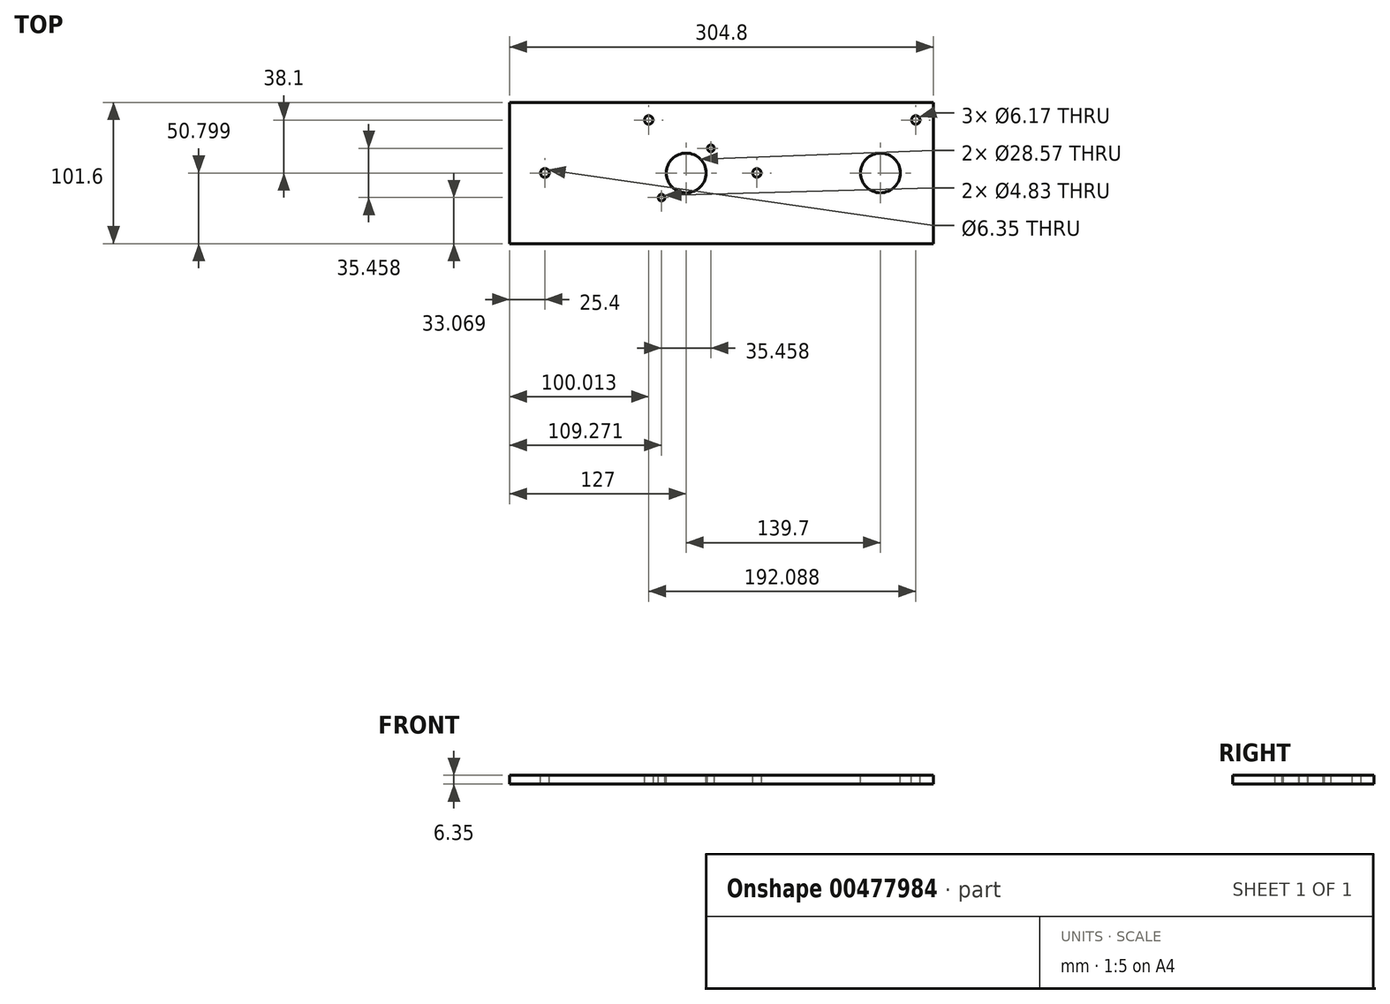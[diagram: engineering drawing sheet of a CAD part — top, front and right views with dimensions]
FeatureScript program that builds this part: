
annotation { "Feature Type Name" : "Feature", "Feature Type Description" : "" }
export const myFeature = defineFeature(function(context is Context, id is Id, definition is map)
    precondition{}
    {
        {
            var Q0;
            Q0=qCreatedBy(makeId("Top.planeOp"),FACE);
            var sketch = newSketch(context, id + "F0", { "sketchPlane" : qUnion([Q0])});
            skLineSegment(sketch, "E0.bottom", {"start": v(-72.69, 42.63) * mm, "end": v(232.11, 42.63) * mm});
            skLineSegment(sketch, "E0.top", {"start": v(-72.69, -58.97) * mm, "end": v(232.11, -58.97) * mm});
            skLineSegment(sketch, "E0.left", {"start": v(-72.69, 42.63) * mm, "end": v(-72.69, -58.97) * mm});
            skLineSegment(sketch, "E0.right", {"start": v(232.11, 42.63) * mm, "end": v(232.11, -58.97) * mm});
            skSolve(sketch);
        }
        {
            var Q0;
            Q0=makeQuery(id+"F0.imprint","IMPRINT",FACE,{"disambiguationData":[TD([[makeQuery(id+"F0.imprint","IMPRINT",EDGE,{"derivedFrom":sQuery(id+"F0.wireOp",EDGE,"E0.bottom")}),-1.0]])]});
            extrude(context, id + "F1", {"entities" : qUnion([Q0]), "depth" : 6.35 * mm});
        }
        {
            var Q0;
            Q0=makeQuery(id+"F1.opExtrude","CAP_FACE",FACE,{"disambiguationData":[OSD([sQuery(id+"F0.wireOp",EDGE,"E0.bottom"),sQuery(id+"F0.wireOp",EDGE,"E0.top"),sQuery(id+"F0.wireOp",EDGE,"E0.left"),sQuery(id+"F0.wireOp",EDGE,"E0.right")])],"isStart":false});
            var sketch = newSketch(context, id + "F2", { "sketchPlane" : qUnion([Q0])});
            skPoint(sketch, "E1", {"position": v(-47.29, -8.17) * mm});
            skCircle(sketch, "E2", {"center": v(-47.29, -8.17) * mm, "radius": 3.18 * mm});
            skSolve(sketch);
        }
        {
            var Q0;
            Q0=makeQuery(id+"F2.imprint","IMPRINT",FACE,{"disambiguationData":[TD([[makeQuery(id+"F2.imprint","IMPRINT",EDGE,{"derivedFrom":sQuery(id+"F2.wireOp",EDGE,"E2")}),1.0]])]});
            extrude(context, id + "F3", {"entities" : qUnion([Q0]), "operationType" : NewBodyOperationType.REMOVE, "oppositeDirection" : true, "depth" : 6.35 * mm});
        }
        {
            var Q0;
            Q0=makeQuery(id+"F2.imprint","IMPRINT",FACE,{"disambiguationData":[TD([[makeQuery(id+"F2.imprint","IMPRINT",EDGE,{"derivedFrom":sQuery(id+"F2.wireOp",EDGE,"E2")}),-1.0]])]});
            var sketch = newSketch(context, id + "F4", { "sketchPlane" : qUnion([Q0])});
            skCircle(sketch, "E3", {"center": v(194.01, -8.17) * mm, "radius": 14.29 * mm});
            skSolve(sketch);
        }
        {
            var Q0;
            Q0=makeQuery(id+"F4.imprint","IMPRINT",FACE,{"disambiguationData":[TD([[makeQuery(id+"F4.imprint","IMPRINT",EDGE,{"derivedFrom":sQuery(id+"F4.wireOp",EDGE,"E3")}),1.0]])]});
            extrude(context, id + "F5", {"entities" : qUnion([Q0]), "operationType" : NewBodyOperationType.REMOVE, "oppositeDirection" : true, "depth" : 6.35 * mm});
        }
        {
            var Q0;
            Q0=makeQuery(id+"F1.opExtrude","CAP_FACE",FACE,{"disambiguationData":[OSD([sQuery(id+"F0.wireOp",EDGE,"E0.bottom"),sQuery(id+"F0.wireOp",EDGE,"E0.top"),sQuery(id+"F0.wireOp",EDGE,"E0.left"),sQuery(id+"F0.wireOp",EDGE,"E0.right")])],"isStart":false});
            var sketch = newSketch(context, id + "F6", { "sketchPlane" : qUnion([Q0])});
            skCircle(sketch, "E4", {"center": v(54.31, -8.17) * mm, "radius": 14.29 * mm});
            skSolve(sketch);
        }
        {
            var Q0;
            Q0=makeQuery(id+"F6.imprint","IMPRINT",FACE,{"disambiguationData":[TD([[makeQuery(id+"F6.imprint","IMPRINT",EDGE,{"derivedFrom":sQuery(id+"F6.wireOp",EDGE,"E4")}),1.0]])]});
            extrude(context, id + "F7", {"entities" : qUnion([Q0]), "operationType" : NewBodyOperationType.REMOVE, "oppositeDirection" : true, "depth" : 6.35 * mm});
        }
        {
            var Q0;
            Q0=makeQuery(id+"F1.opExtrude","CAP_FACE",FACE,{"disambiguationData":[OSD([sQuery(id+"F0.wireOp",EDGE,"E0.bottom"),sQuery(id+"F0.wireOp",EDGE,"E0.top"),sQuery(id+"F0.wireOp",EDGE,"E0.left"),sQuery(id+"F0.wireOp",EDGE,"E0.right")])],"isStart":false});
            var sketch = newSketch(context, id + "F8", { "sketchPlane" : qUnion([Q0])});
            skLineSegment(sketch, "E5.bottom", {"start": v(33.3, 14.05) * mm, "end": v(75.32, 14.05) * mm});
            skLineSegment(sketch, "E5.top", {"start": v(33.3, -30.4) * mm, "end": v(75.32, -30.4) * mm});
            skLineSegment(sketch, "E5.left", {"start": v(33.3, 14.05) * mm, "end": v(33.3, -30.4) * mm});
            skLineSegment(sketch, "E5.right", {"start": v(75.32, 14.05) * mm, "end": v(75.32, -30.4) * mm});
            skSolve(sketch);
        }
        {
            var Q0;
            Q0=makeQuery(id+"F8.imprint","IMPRINT",FACE,{"disambiguationData":[TD([[makeQuery(id+"F8.imprint","IMPRINT",EDGE,{"derivedFrom":sQuery(id+"F8.wireOp",EDGE,"E5.bottom")}),-1.0]])]});
            var sketch = newSketch(context, id + "F9", { "sketchPlane" : qUnion([Q0])});
            skCircle(sketch, "E6", {"center": v(36.58, -25.9) * mm, "radius": 2.41 * mm});
            skCircle(sketch, "E7", {"center": v(72.04, 9.56) * mm, "radius": 2.41 * mm});
            skSolve(sketch);
        }
        {
            var Q0;
            Q0=qSketchRegion(id+"F9",true);
            extrude(context, id + "F10", {"entities" : qUnion([Q0]), "operationType" : NewBodyOperationType.REMOVE, "oppositeDirection" : true, "depth" : 6.35 * mm});
        }
        {
            var Q0;
            Q0=makeQuery(id+"F0.imprint","IMPRINT",FACE,{"disambiguationData":[TD([[makeQuery(id+"F0.imprint","IMPRINT",EDGE,{"derivedFrom":sQuery(id+"F0.wireOp",EDGE,"E0.bottom")}),-1.0]])]});
            var sketch = newSketch(context, id + "F11", { "sketchPlane" : qUnion([Q0])});
            skCircle(sketch, "E8", {"center": v(105.11, -8.17) * mm, "radius": 3.09 * mm});
            skSolve(sketch);
        }
        {
            var Q0;
            Q0=makeQuery(id+"F11.imprint","IMPRINT",FACE,{"disambiguationData":[TD([[makeQuery(id+"F11.imprint","IMPRINT",EDGE,{"derivedFrom":sQuery(id+"F11.wireOp",EDGE,"E8")}),1.0]])]});
            extrude(context, id + "F12", {"entities" : qUnion([Q0]), "operationType" : NewBodyOperationType.REMOVE, "depth" : 6.35 * mm});
        }
        {
            var Q0;
            Q0=makeQuery(id+"F0.imprint","IMPRINT",FACE,{"disambiguationData":[TD([[makeQuery(id+"F0.imprint","IMPRINT",EDGE,{"derivedFrom":sQuery(id+"F0.wireOp",EDGE,"E0.bottom")}),-1.0]])]});
            var sketch = newSketch(context, id + "F13", { "sketchPlane" : qUnion([Q0])});
            skCircle(sketch, "E9", {"center": v(27.32, 29.93) * mm, "radius": 3.09 * mm});
            skSolve(sketch);
        }
        {
            var Q0;
            Q0=makeQuery(id+"F13.imprint","IMPRINT",FACE,{"disambiguationData":[TD([[makeQuery(id+"F13.imprint","IMPRINT",EDGE,{"derivedFrom":sQuery(id+"F13.wireOp",EDGE,"E9")}),1.0]])]});
            extrude(context, id + "F14", {"entities" : qUnion([Q0]), "operationType" : NewBodyOperationType.REMOVE, "depth" : 6.35 * mm});
        }
        {
            var Q0;
            Q0=makeQuery(id+"F8.imprint","IMPRINT",FACE,{"disambiguationData":[TD([[makeQuery(id+"F8.imprint","IMPRINT",EDGE,{"derivedFrom":sQuery(id+"F8.wireOp",EDGE,"E5.bottom")}),1.0]])]});
            var sketch = newSketch(context, id + "F15", { "sketchPlane" : qUnion([Q0])});
            skCircle(sketch, "E10", {"center": v(219.41, 29.93) * mm, "radius": 3.09 * mm});
            skSolve(sketch);
        }
        {
            var Q0;
            Q0=makeQuery(id+"F15.imprint","IMPRINT",FACE,{"disambiguationData":[TD([[makeQuery(id+"F15.imprint","IMPRINT",EDGE,{"derivedFrom":sQuery(id+"F15.wireOp",EDGE,"E10")}),1.0]])]});
            extrude(context, id + "F16", {"entities" : qUnion([Q0]), "operationType" : NewBodyOperationType.REMOVE, "oppositeDirection" : true, "depth" : 6.35 * mm});
        }
    });
